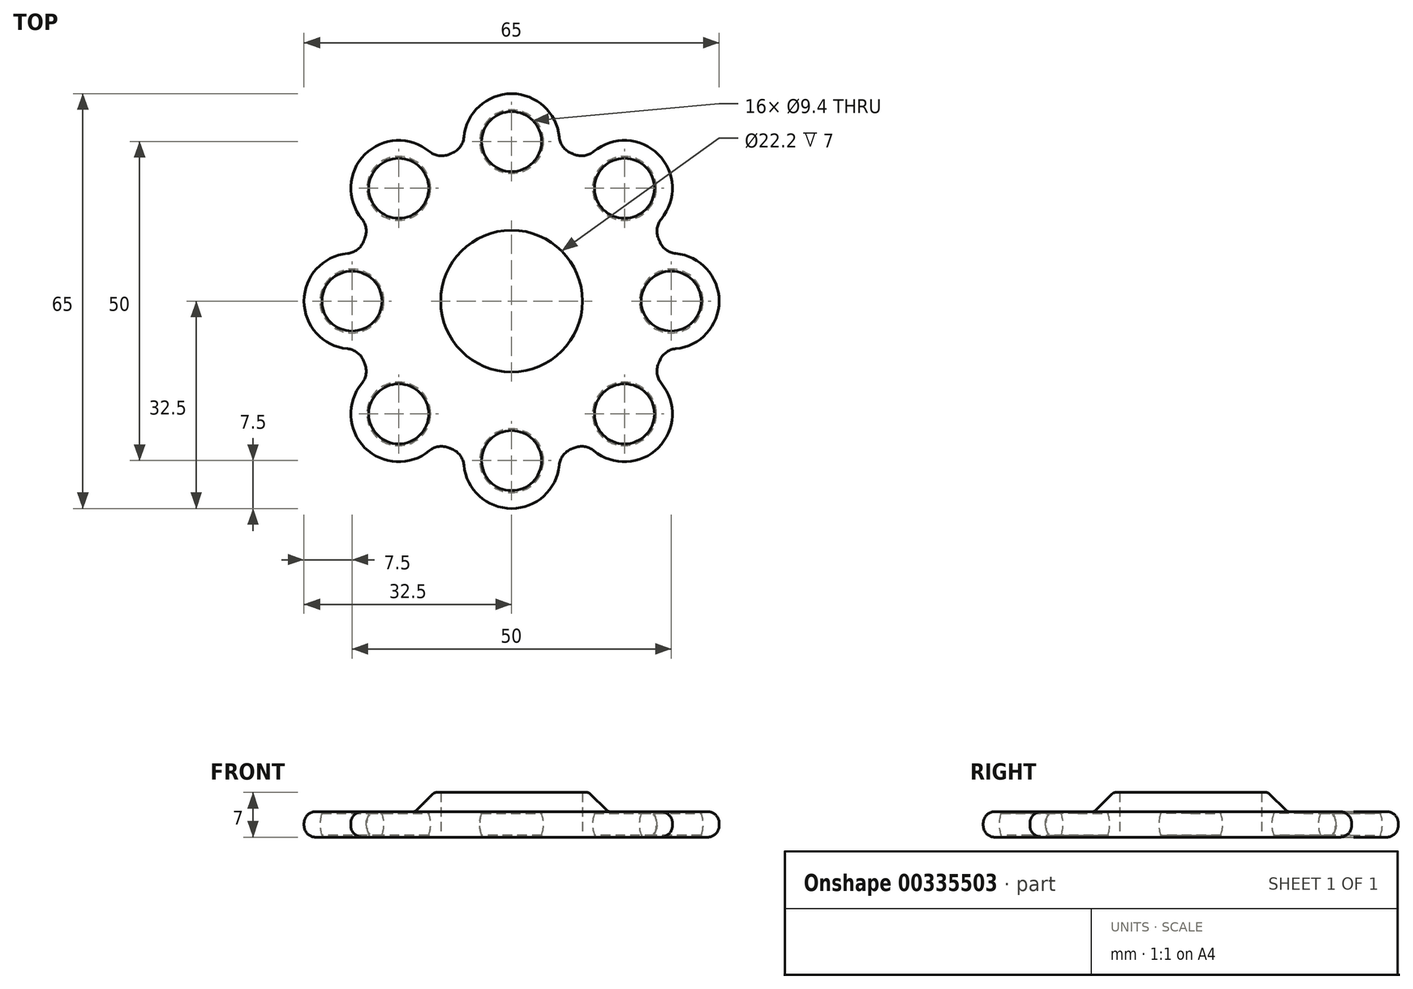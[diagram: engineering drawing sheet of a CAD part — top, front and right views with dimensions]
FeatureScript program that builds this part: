
annotation { "Feature Type Name" : "Feature", "Feature Type Description" : "" }
export const myFeature = defineFeature(function(context is Context, id is Id, definition is map)
    precondition{}
    {
        {
            var Q0;
            Q0=qCreatedBy(makeId("Top.planeOp"),FACE);
            var sketch = newSketch(context, id + "F0", { "sketchPlane" : qUnion([Q0])});
            skCircle(sketch, "E0", {"center": v(0, 0) * mm, "radius": 11.1 * mm});
            skPoint(sketch, "E1.0.midPoint", {"position": v(12.23, 6.82) * mm});
            skCircle(sketch, "E2", {"center": v(0, 25) * mm, "radius": 4.7 * mm});
            skCircle(sketch, "E3.1.0", {"center": v(-17.68, 17.68) * mm, "radius": 4.7 * mm});
            skCircle(sketch, "E3.2.0", {"center": v(-25, 0) * mm, "radius": 4.7 * mm});
            skCircle(sketch, "E3.3.0", {"center": v(-17.68, -17.68) * mm, "radius": 4.7 * mm});
            skCircle(sketch, "E3.4.0", {"center": v(0, -25) * mm, "radius": 4.7 * mm});
            skCircle(sketch, "E3.5.0", {"center": v(17.68, -17.68) * mm, "radius": 4.7 * mm});
            skCircle(sketch, "E3.6.0", {"center": v(25, 0) * mm, "radius": 4.7 * mm});
            skCircle(sketch, "E3.7.0", {"center": v(17.68, 17.68) * mm, "radius": 4.7 * mm});
            skCircle(sketch, "E4", {"center": v(0, 25) * mm, "radius": 7.5 * mm});
            skCircle(sketch, "E5.1.0", {"center": v(-17.68, 17.68) * mm, "radius": 7.5 * mm});
            skCircle(sketch, "E5.2.0", {"center": v(-25, 0) * mm, "radius": 7.5 * mm});
            skCircle(sketch, "E5.3.0", {"center": v(-17.68, -17.68) * mm, "radius": 7.5 * mm});
            skCircle(sketch, "E5.4.0", {"center": v(0, -25) * mm, "radius": 7.5 * mm});
            skCircle(sketch, "E5.5.0", {"center": v(17.68, -17.68) * mm, "radius": 7.5 * mm});
            skCircle(sketch, "E5.6.0", {"center": v(25, 0) * mm, "radius": 7.5 * mm});
            skCircle(sketch, "E5.7.0", {"center": v(17.68, 17.68) * mm, "radius": 7.5 * mm});
            skCircle(sketch, "E6", {"center": v(0, 0) * mm, "radius": 25 * mm});
            skSolve(sketch);
        }
        {
            var Q0;
            Q0=makeQuery(id+"F0.imprint","IMPRINT",FACE,{"disambiguationData":[TD([[makeQuery(id+"F0.imprint","IMPRINT",EDGE,{"derivedFrom":sQuery(id+"F0.wireOp",EDGE,"E0")}),-1.0]])]});
            var Q1;
            {var subQ0=sQuery(id+"F0.wireOp",EDGE,"E6");var subQ1=sQuery(id+"F0.wireOp",EDGE,"E3.3.0");var subQ2=makeQuery(id+"F0.imprint","INTERSECT",VERTEX,{"disambiguationData":[OD(0.0)],"derivedFrom":[subQ1,subQ0]});Q1=makeQuery(id+"F0.imprint","IMPRINT",FACE,{"disambiguationData":[TD([[makeQuery(id+"F0.imprint","IMPRINT",EDGE,{"disambiguationData":[TD([[subQ2,-1.0]])],"derivedFrom":subQ1}),-1.0]])]});}
            var Q2;
            {var subQ0=sQuery(id+"F0.wireOp",EDGE,"E6");var subQ1=sQuery(id+"F0.wireOp",EDGE,"E3.3.0");var subQ2=makeQuery(id+"F0.imprint","INTERSECT",VERTEX,{"disambiguationData":[OD(0.0)],"derivedFrom":[subQ1,subQ0]});Q2=makeQuery(id+"F0.imprint","IMPRINT",FACE,{"disambiguationData":[TD([[makeQuery(id+"F0.imprint","IMPRINT",EDGE,{"disambiguationData":[TD([[subQ2,1.0]])],"derivedFrom":subQ1}),-1.0]])]});}
            var Q3;
            {var subQ0=sQuery(id+"F0.wireOp",EDGE,"E6");var subQ1=sQuery(id+"F0.wireOp",EDGE,"E3.2.0");var subQ2=makeQuery(id+"F0.imprint","INTERSECT",VERTEX,{"disambiguationData":[OD(0.0)],"derivedFrom":[subQ1,subQ0]});Q3=makeQuery(id+"F0.imprint","IMPRINT",FACE,{"disambiguationData":[TD([[makeQuery(id+"F0.imprint","IMPRINT",EDGE,{"disambiguationData":[TD([[subQ2,1.0]])],"derivedFrom":subQ1}),-1.0]])]});}
            var Q4;
            {var subQ0=sQuery(id+"F0.wireOp",EDGE,"E6");var subQ1=sQuery(id+"F0.wireOp",EDGE,"E3.2.0");var subQ2=makeQuery(id+"F0.imprint","INTERSECT",VERTEX,{"disambiguationData":[OD(0.0)],"derivedFrom":[subQ1,subQ0]});Q4=makeQuery(id+"F0.imprint","IMPRINT",FACE,{"disambiguationData":[TD([[makeQuery(id+"F0.imprint","IMPRINT",EDGE,{"disambiguationData":[TD([[subQ2,-1.0]])],"derivedFrom":subQ1}),-1.0]])]});}
            var Q5;
            {var subQ0=sQuery(id+"F0.wireOp",EDGE,"E6");var subQ1=sQuery(id+"F0.wireOp",EDGE,"E3.1.0");var subQ2=makeQuery(id+"F0.imprint","INTERSECT",VERTEX,{"disambiguationData":[OD(0.0)],"derivedFrom":[subQ1,subQ0]});Q5=makeQuery(id+"F0.imprint","IMPRINT",FACE,{"disambiguationData":[TD([[makeQuery(id+"F0.imprint","IMPRINT",EDGE,{"disambiguationData":[TD([[subQ2,-1.0]])],"derivedFrom":subQ1}),-1.0]])]});}
            var Q6;
            {var subQ0=sQuery(id+"F0.wireOp",EDGE,"E6");var subQ1=sQuery(id+"F0.wireOp",EDGE,"E3.1.0");var subQ2=makeQuery(id+"F0.imprint","INTERSECT",VERTEX,{"disambiguationData":[OD(0.0)],"derivedFrom":[subQ1,subQ0]});Q6=makeQuery(id+"F0.imprint","IMPRINT",FACE,{"disambiguationData":[TD([[makeQuery(id+"F0.imprint","IMPRINT",EDGE,{"disambiguationData":[TD([[subQ2,1.0]])],"derivedFrom":subQ1}),-1.0]])]});}
            var Q7;
            {var subQ0=sQuery(id+"F0.wireOp",EDGE,"E6");var subQ1=sQuery(id+"F0.wireOp",EDGE,"E2");var subQ2=makeQuery(id+"F0.imprint","INTERSECT",VERTEX,{"disambiguationData":[OD(0.0)],"derivedFrom":[subQ1,subQ0]});Q7=makeQuery(id+"F0.imprint","IMPRINT",FACE,{"disambiguationData":[TD([[makeQuery(id+"F0.imprint","IMPRINT",EDGE,{"disambiguationData":[TD([[subQ2,1.0]])],"derivedFrom":subQ1}),-1.0]])]});}
            var Q8;
            {var subQ0=sQuery(id+"F0.wireOp",EDGE,"E6");var subQ1=sQuery(id+"F0.wireOp",EDGE,"E2");var subQ2=makeQuery(id+"F0.imprint","INTERSECT",VERTEX,{"disambiguationData":[OD(0.0)],"derivedFrom":[subQ1,subQ0]});Q8=makeQuery(id+"F0.imprint","IMPRINT",FACE,{"disambiguationData":[TD([[makeQuery(id+"F0.imprint","IMPRINT",EDGE,{"disambiguationData":[TD([[subQ2,-1.0]])],"derivedFrom":subQ1}),-1.0]])]});}
            var Q9;
            {var subQ0=sQuery(id+"F0.wireOp",EDGE,"E6");var subQ1=sQuery(id+"F0.wireOp",EDGE,"E3.7.0");var subQ2=makeQuery(id+"F0.imprint","INTERSECT",VERTEX,{"disambiguationData":[OD(0.0)],"derivedFrom":[subQ1,subQ0]});Q9=makeQuery(id+"F0.imprint","IMPRINT",FACE,{"disambiguationData":[TD([[makeQuery(id+"F0.imprint","IMPRINT",EDGE,{"disambiguationData":[TD([[subQ2,1.0]])],"derivedFrom":subQ1}),-1.0]])]});}
            var Q10;
            {var subQ0=sQuery(id+"F0.wireOp",EDGE,"E6");var subQ1=sQuery(id+"F0.wireOp",EDGE,"E3.7.0");var subQ2=makeQuery(id+"F0.imprint","INTERSECT",VERTEX,{"disambiguationData":[OD(0.0)],"derivedFrom":[subQ1,subQ0]});Q10=makeQuery(id+"F0.imprint","IMPRINT",FACE,{"disambiguationData":[TD([[makeQuery(id+"F0.imprint","IMPRINT",EDGE,{"disambiguationData":[TD([[subQ2,-1.0]])],"derivedFrom":subQ1}),-1.0]])]});}
            var Q11;
            {var subQ0=sQuery(id+"F0.wireOp",EDGE,"E6");var subQ1=sQuery(id+"F0.wireOp",EDGE,"E3.6.0");var subQ2=makeQuery(id+"F0.imprint","INTERSECT",VERTEX,{"disambiguationData":[OD(0.0)],"derivedFrom":[subQ1,subQ0]});Q11=makeQuery(id+"F0.imprint","IMPRINT",FACE,{"disambiguationData":[TD([[makeQuery(id+"F0.imprint","IMPRINT",EDGE,{"disambiguationData":[TD([[subQ2,-1.0]])],"derivedFrom":subQ1}),-1.0]])]});}
            var Q12;
            {var subQ0=sQuery(id+"F0.wireOp",EDGE,"E6");var subQ1=sQuery(id+"F0.wireOp",EDGE,"E3.6.0");var subQ2=makeQuery(id+"F0.imprint","INTERSECT",VERTEX,{"disambiguationData":[OD(0.0)],"derivedFrom":[subQ1,subQ0]});Q12=makeQuery(id+"F0.imprint","IMPRINT",FACE,{"disambiguationData":[TD([[makeQuery(id+"F0.imprint","IMPRINT",EDGE,{"disambiguationData":[TD([[subQ2,1.0]])],"derivedFrom":subQ1}),-1.0]])]});}
            var Q13;
            {var subQ0=sQuery(id+"F0.wireOp",EDGE,"E6");var subQ1=sQuery(id+"F0.wireOp",EDGE,"E3.5.0");var subQ2=makeQuery(id+"F0.imprint","INTERSECT",VERTEX,{"disambiguationData":[OD(0.0)],"derivedFrom":[subQ1,subQ0]});Q13=makeQuery(id+"F0.imprint","IMPRINT",FACE,{"disambiguationData":[TD([[makeQuery(id+"F0.imprint","IMPRINT",EDGE,{"disambiguationData":[TD([[subQ2,1.0]])],"derivedFrom":subQ1}),-1.0]])]});}
            var Q14;
            {var subQ0=sQuery(id+"F0.wireOp",EDGE,"E6");var subQ1=sQuery(id+"F0.wireOp",EDGE,"E3.5.0");var subQ2=makeQuery(id+"F0.imprint","INTERSECT",VERTEX,{"disambiguationData":[OD(0.0)],"derivedFrom":[subQ1,subQ0]});Q14=makeQuery(id+"F0.imprint","IMPRINT",FACE,{"disambiguationData":[TD([[makeQuery(id+"F0.imprint","IMPRINT",EDGE,{"disambiguationData":[TD([[subQ2,-1.0]])],"derivedFrom":subQ1}),-1.0]])]});}
            var Q15;
            {var subQ0=sQuery(id+"F0.wireOp",EDGE,"E6");var subQ1=sQuery(id+"F0.wireOp",EDGE,"E3.4.0");var subQ2=makeQuery(id+"F0.imprint","INTERSECT",VERTEX,{"disambiguationData":[OD(0.0)],"derivedFrom":[subQ1,subQ0]});Q15=makeQuery(id+"F0.imprint","IMPRINT",FACE,{"disambiguationData":[TD([[makeQuery(id+"F0.imprint","IMPRINT",EDGE,{"disambiguationData":[TD([[subQ2,1.0]])],"derivedFrom":subQ1}),-1.0]])]});}
            var Q16;
            {var subQ0=sQuery(id+"F0.wireOp",EDGE,"E6");var subQ1=sQuery(id+"F0.wireOp",EDGE,"E3.4.0");var subQ2=makeQuery(id+"F0.imprint","INTERSECT",VERTEX,{"disambiguationData":[OD(0.0)],"derivedFrom":[subQ1,subQ0]});Q16=makeQuery(id+"F0.imprint","IMPRINT",FACE,{"disambiguationData":[TD([[makeQuery(id+"F0.imprint","IMPRINT",EDGE,{"disambiguationData":[TD([[subQ2,-1.0]])],"derivedFrom":subQ1}),-1.0]])]});}
            extrude(context, id + "F1", {"entities" : qUnion([Q0, Q1, Q2, Q3, Q4, Q5, Q6, Q7, Q8, Q9, Q10, Q11, Q12, Q13, Q14, Q15, Q16]), "depth" : 2 * mm, "hasSecondDirection" : true, "secondDirectionOppositeDirection" : true, "secondDirectionDepth" : 2 * mm});
        }
        {
            var Q0;
            {var subQ0=sQuery(id+"F0.wireOp",EDGE,"E6");var subQ1=sQuery(id+"F0.wireOp",EDGE,"E5.4.0");Q0=makeQuery(id+"F1.opExtrude","SWEPT_EDGE",EDGE,{"disambiguationData":[OSD([subQ1,subQ0]),TDD([makeQuery(id+"F0.imprint","INTERSECT",VERTEX,{"disambiguationData":[OD(0.0)],"derivedFrom":[subQ1,subQ0]})])]});}
            var Q1;
            {var subQ0=sQuery(id+"F0.wireOp",EDGE,"E6");var subQ1=sQuery(id+"F0.wireOp",EDGE,"E5.2.0");Q1=makeQuery(id+"F1.opExtrude","SWEPT_EDGE",EDGE,{"disambiguationData":[OSD([subQ1,subQ0]),TDD([makeQuery(id+"F0.imprint","INTERSECT",VERTEX,{"disambiguationData":[OD(1.0)],"derivedFrom":[subQ1,subQ0]})])]});}
            var Q2;
            {var subQ0=sQuery(id+"F0.wireOp",EDGE,"E6");var subQ1=sQuery(id+"F0.wireOp",EDGE,"E5.2.0");Q2=makeQuery(id+"F1.opExtrude","SWEPT_EDGE",EDGE,{"disambiguationData":[OSD([subQ1,subQ0]),TDD([makeQuery(id+"F0.imprint","INTERSECT",VERTEX,{"disambiguationData":[OD(0.0)],"derivedFrom":[subQ1,subQ0]})])]});}
            var Q3;
            {var subQ0=sQuery(id+"F0.wireOp",EDGE,"E6");var subQ1=sQuery(id+"F0.wireOp",EDGE,"E4");Q3=makeQuery(id+"F1.opExtrude","SWEPT_EDGE",EDGE,{"disambiguationData":[OSD([subQ1,subQ0]),TDD([makeQuery(id+"F0.imprint","INTERSECT",VERTEX,{"disambiguationData":[OD(1.0)],"derivedFrom":[subQ1,subQ0]})])]});}
            var Q4;
            {var subQ0=sQuery(id+"F0.wireOp",EDGE,"E6");var subQ1=sQuery(id+"F0.wireOp",EDGE,"E5.7.0");Q4=makeQuery(id+"F1.opExtrude","SWEPT_EDGE",EDGE,{"disambiguationData":[OSD([subQ1,subQ0]),TDD([makeQuery(id+"F0.imprint","INTERSECT",VERTEX,{"disambiguationData":[OD(1.0)],"derivedFrom":[subQ1,subQ0]})])]});}
            var Q5;
            {var subQ0=sQuery(id+"F0.wireOp",EDGE,"E6");var subQ1=sQuery(id+"F0.wireOp",EDGE,"E5.1.0");Q5=makeQuery(id+"F1.opExtrude","SWEPT_EDGE",EDGE,{"disambiguationData":[OSD([subQ1,subQ0]),TDD([makeQuery(id+"F0.imprint","INTERSECT",VERTEX,{"disambiguationData":[OD(1.0)],"derivedFrom":[subQ1,subQ0]})])]});}
            var Q6;
            {var subQ0=sQuery(id+"F0.wireOp",EDGE,"E6");var subQ1=sQuery(id+"F0.wireOp",EDGE,"E5.3.0");Q6=makeQuery(id+"F1.opExtrude","SWEPT_EDGE",EDGE,{"disambiguationData":[OSD([subQ1,subQ0]),TDD([makeQuery(id+"F0.imprint","INTERSECT",VERTEX,{"disambiguationData":[OD(0.0)],"derivedFrom":[subQ1,subQ0]})])]});}
            var Q7;
            {var subQ0=sQuery(id+"F0.wireOp",EDGE,"E6");var subQ1=sQuery(id+"F0.wireOp",EDGE,"E5.1.0");Q7=makeQuery(id+"F1.opExtrude","SWEPT_EDGE",EDGE,{"disambiguationData":[OSD([subQ1,subQ0]),TDD([makeQuery(id+"F0.imprint","INTERSECT",VERTEX,{"disambiguationData":[OD(0.0)],"derivedFrom":[subQ1,subQ0]})])]});}
            var Q8;
            {var subQ0=sQuery(id+"F0.wireOp",EDGE,"E6");var subQ1=sQuery(id+"F0.wireOp",EDGE,"E4");Q8=makeQuery(id+"F1.opExtrude","SWEPT_EDGE",EDGE,{"disambiguationData":[OSD([subQ1,subQ0]),TDD([makeQuery(id+"F0.imprint","INTERSECT",VERTEX,{"disambiguationData":[OD(0.0)],"derivedFrom":[subQ1,subQ0]})])]});}
            var Q9;
            {var subQ0=sQuery(id+"F0.wireOp",EDGE,"E6");var subQ1=sQuery(id+"F0.wireOp",EDGE,"E5.6.0");Q9=makeQuery(id+"F1.opExtrude","SWEPT_EDGE",EDGE,{"disambiguationData":[OSD([subQ1,subQ0]),TDD([makeQuery(id+"F0.imprint","INTERSECT",VERTEX,{"disambiguationData":[OD(0.0)],"derivedFrom":[subQ1,subQ0]})])]});}
            var Q10;
            {var subQ0=sQuery(id+"F0.wireOp",EDGE,"E6");var subQ1=sQuery(id+"F0.wireOp",EDGE,"E5.7.0");Q10=makeQuery(id+"F1.opExtrude","SWEPT_EDGE",EDGE,{"disambiguationData":[OSD([subQ1,subQ0]),TDD([makeQuery(id+"F0.imprint","INTERSECT",VERTEX,{"disambiguationData":[OD(0.0)],"derivedFrom":[subQ1,subQ0]})])]});}
            var Q11;
            {var subQ0=sQuery(id+"F0.wireOp",EDGE,"E6");var subQ1=sQuery(id+"F0.wireOp",EDGE,"E5.6.0");Q11=makeQuery(id+"F1.opExtrude","SWEPT_EDGE",EDGE,{"disambiguationData":[OSD([subQ1,subQ0]),TDD([makeQuery(id+"F0.imprint","INTERSECT",VERTEX,{"disambiguationData":[OD(1.0)],"derivedFrom":[subQ1,subQ0]})])]});}
            var Q12;
            {var subQ0=sQuery(id+"F0.wireOp",EDGE,"E6");var subQ1=sQuery(id+"F0.wireOp",EDGE,"E5.5.0");Q12=makeQuery(id+"F1.opExtrude","SWEPT_EDGE",EDGE,{"disambiguationData":[OSD([subQ1,subQ0]),TDD([makeQuery(id+"F0.imprint","INTERSECT",VERTEX,{"disambiguationData":[OD(1.0)],"derivedFrom":[subQ1,subQ0]})])]});}
            var Q13;
            {var subQ0=sQuery(id+"F0.wireOp",EDGE,"E6");var subQ1=sQuery(id+"F0.wireOp",EDGE,"E5.5.0");Q13=makeQuery(id+"F1.opExtrude","SWEPT_EDGE",EDGE,{"disambiguationData":[OSD([subQ1,subQ0]),TDD([makeQuery(id+"F0.imprint","INTERSECT",VERTEX,{"disambiguationData":[OD(0.0)],"derivedFrom":[subQ1,subQ0]})])]});}
            var Q14;
            {var subQ0=sQuery(id+"F0.wireOp",EDGE,"E6");var subQ1=sQuery(id+"F0.wireOp",EDGE,"E5.4.0");Q14=makeQuery(id+"F1.opExtrude","SWEPT_EDGE",EDGE,{"disambiguationData":[OSD([subQ1,subQ0]),TDD([makeQuery(id+"F0.imprint","INTERSECT",VERTEX,{"disambiguationData":[OD(1.0)],"derivedFrom":[subQ1,subQ0]})])]});}
            var Q15;
            {var subQ0=sQuery(id+"F0.wireOp",EDGE,"E6");var subQ1=sQuery(id+"F0.wireOp",EDGE,"E5.3.0");Q15=makeQuery(id+"F1.opExtrude","SWEPT_EDGE",EDGE,{"disambiguationData":[OSD([subQ1,subQ0]),TDD([makeQuery(id+"F0.imprint","INTERSECT",VERTEX,{"disambiguationData":[OD(1.0)],"derivedFrom":[subQ1,subQ0]})])]});}
            fillet(context, id + "F2", {"entities" : qUnion([Q0, Q1, Q2, Q3, Q4, Q5, Q6, Q7, Q8, Q9, Q10, Q11, Q12, Q13, Q14, Q15]), "radius" : 3 * mm, "tangentPropagation" : true, "allowEdgeOverflow" : false});
        }
        {
            var Q0;
            Q0=makeQuery(id+"F1.opExtrude","CAP_EDGE",EDGE,{"disambiguationData":[OSD([sQuery(id+"F0.wireOp",EDGE,"E5.7.0")])],"isStart":false});
            var Q1;
            Q1=makeQuery(id+"F1.opExtrude","CAP_EDGE",EDGE,{"disambiguationData":[OSD([sQuery(id+"F0.wireOp",EDGE,"E5.7.0")])],"isStart":true});
            fillet(context, id + "F3", {"entities" : qUnion([Q0, Q1]), "radius" : 1.8 * mm, "tangentPropagation" : true, "allowEdgeOverflow" : false});
        }
        {
            var Q0;
            Q0=qCreatedBy(makeId("Right.planeOp"),FACE);
            var sketch = newSketch(context, id + "F4", { "sketchPlane" : qUnion([Q0])});
            skPoint(sketch, "E7.0", {"position": v(-25, 0) * mm});
            skPoint(sketch, "E7.1", {"position": v(25, 0) * mm});
            skLineSegment(sketch, "E8", {"start": v(-25, 12.35) * mm, "end": v(-25, -14.21) * mm, "construction": true});
            skLineSegment(sketch, "E9", {"start": v(25, 12.16) * mm, "end": v(25, -14.21) * mm, "construction": true});
            skPoint(sketch, "E10", {"position": v(-25, 5) * mm});
            skPoint(sketch, "E11", {"position": v(-25, -5) * mm});
            skPoint(sketch, "E12", {"position": v(25, 5) * mm});
            skPoint(sketch, "E13", {"position": v(25, -5) * mm});
            skArc(sketch, "E14", {"start": v(-25, 5) * mm, "mid": v(-30, 0) * mm, "end": v(-25, -5) * mm});
            skArc(sketch, "E15", {"start": v(25, -5) * mm, "mid": v(30, 0) * mm, "end": v(25, 5) * mm});
            skLineSegment(sketch, "E16", {"start": v(-25, 5) * mm, "end": v(-25, -5) * mm});
            skLineSegment(sketch, "E17", {"start": v(25, 5) * mm, "end": v(25, -5) * mm});
            skLineSegment(sketch, "E18", {"start": v(0, 41.23) * mm, "end": v(0, -49.38) * mm, "construction": true});
            skSolve(sketch);
        }
        {
            var Q0;
            Q0=makeQuery(id+"F4.imprint","IMPRINT",FACE,{"disambiguationData":[TD([[makeQuery(id+"F4.imprint","IMPRINT",EDGE,{"derivedFrom":sQuery(id+"F4.wireOp",EDGE,"E14")}),1.0]])]});
            var Q1;
            Q1=sQuery(id+"F4.wireOp",EDGE,"E8");
            revolve(context, id + "F5", {"entities" : qUnion([Q0]), "axis" : qUnion([Q1]), "revolveType" : RevolveType.FULL});
        }
        {
            var Q0;
            Q0=makeQuery(id+"F4.imprint","IMPRINT",FACE,{"disambiguationData":[TD([[makeQuery(id+"F4.imprint","IMPRINT",EDGE,{"derivedFrom":sQuery(id+"F4.wireOp",EDGE,"E15")}),1.0]])]});
            var Q1;
            Q1=sQuery(id+"F4.wireOp",EDGE,"E9");
            revolve(context, id + "F6", {"entities" : qUnion([Q0]), "axis" : qUnion([Q1]), "revolveType" : RevolveType.FULL});
        }
        {
            var Q0;
            Q0=makeQuery(id+"F6.opRevolve","SWEPT_BODY",BODY,{"disambiguationData":[OSD([sQuery(id+"F4.wireOp",EDGE,"E15"),sQuery(id+"F4.wireOp",EDGE,"E17")])]});
            var Q1;
            Q1=makeQuery(id+"F5.opRevolve","SWEPT_BODY",BODY,{"disambiguationData":[OSD([sQuery(id+"F4.wireOp",EDGE,"E14"),sQuery(id+"F4.wireOp",EDGE,"E16")])]});
            var Q2;
            Q2=makeQuery(id+"F1.opExtrude","SWEPT_BODY",BODY,{"disambiguationData":[OSD([sQuery(id+"F0.wireOp",EDGE,"E0"),sQuery(id+"F0.wireOp",EDGE,"E2"),sQuery(id+"F0.wireOp",EDGE,"E3.1.0"),sQuery(id+"F0.wireOp",EDGE,"E3.2.0"),sQuery(id+"F0.wireOp",EDGE,"E3.3.0"),sQuery(id+"F0.wireOp",EDGE,"E3.4.0"),sQuery(id+"F0.wireOp",EDGE,"E3.5.0"),sQuery(id+"F0.wireOp",EDGE,"E3.6.0"),sQuery(id+"F0.wireOp",EDGE,"E3.7.0"),sQuery(id+"F0.wireOp",EDGE,"E4"),sQuery(id+"F0.wireOp",EDGE,"E5.1.0"),sQuery(id+"F0.wireOp",EDGE,"E5.2.0"),sQuery(id+"F0.wireOp",EDGE,"E5.3.0"),sQuery(id+"F0.wireOp",EDGE,"E5.4.0"),sQuery(id+"F0.wireOp",EDGE,"E5.5.0"),sQuery(id+"F0.wireOp",EDGE,"E5.6.0"),sQuery(id+"F0.wireOp",EDGE,"E5.7.0"),sQuery(id+"F0.wireOp",EDGE,"E6")])]});
            booleanBodies(context, id + "F7", {"operationType" : BooleanOperationType.SUBTRACTION, "tools" : qUnion([Q0, Q1]), "targets" : qUnion([Q2])});
        }
        {
            var Q0;
            Q0=qCreatedBy(makeId("Front.planeOp"),FACE);
            var sketch = newSketch(context, id + "F8", { "sketchPlane" : qUnion([Q0])});
            skPoint(sketch, "E19.0", {"position": v(-25, 0) * mm});
            skPoint(sketch, "E19.1", {"position": v(25, 0) * mm});
            skLineSegment(sketch, "E20", {"start": v(-25, 18.9) * mm, "end": v(-25, -20.91) * mm, "construction": true});
            skLineSegment(sketch, "E21", {"start": v(25, 20.02) * mm, "end": v(25, -22.02) * mm, "construction": true});
            skPoint(sketch, "E22", {"position": v(-25, 5) * mm});
            skPoint(sketch, "E23", {"position": v(-25, -5) * mm});
            skPoint(sketch, "E24", {"position": v(25, 5) * mm});
            skPoint(sketch, "E25", {"position": v(25, -5) * mm});
            skArc(sketch, "E26", {"start": v(-25, 5) * mm, "mid": v(-30, 0) * mm, "end": v(-25, -5) * mm});
            skArc(sketch, "E27", {"start": v(25, -5) * mm, "mid": v(30, 0) * mm, "end": v(25, 5) * mm});
            skLineSegment(sketch, "E28", {"start": v(-25, 5) * mm, "end": v(-25, -5) * mm});
            skLineSegment(sketch, "E29", {"start": v(25, 5) * mm, "end": v(25, -5) * mm});
            skSolve(sketch);
        }
        {
            var Q0;
            Q0=makeQuery(id+"F8.imprint","IMPRINT",FACE,{"disambiguationData":[TD([[makeQuery(id+"F8.imprint","IMPRINT",EDGE,{"derivedFrom":sQuery(id+"F8.wireOp",EDGE,"E26")}),1.0]])]});
            var Q1;
            Q1=sQuery(id+"F8.wireOp",EDGE,"E20");
            revolve(context, id + "F9", {"entities" : qUnion([Q0]), "axis" : qUnion([Q1]), "revolveType" : RevolveType.FULL});
        }
        {
            var Q0;
            Q0=makeQuery(id+"F8.imprint","IMPRINT",FACE,{"disambiguationData":[TD([[makeQuery(id+"F8.imprint","IMPRINT",EDGE,{"derivedFrom":sQuery(id+"F8.wireOp",EDGE,"E27")}),1.0]])]});
            var Q1;
            Q1=sQuery(id+"F8.wireOp",EDGE,"E21");
            revolve(context, id + "F10", {"entities" : qUnion([Q0]), "axis" : qUnion([Q1]), "revolveType" : RevolveType.FULL});
        }
        {
            var Q0;
            Q0=makeQuery(id+"F9.opRevolve","SWEPT_BODY",BODY,{"disambiguationData":[OSD([sQuery(id+"F8.wireOp",EDGE,"E26"),sQuery(id+"F8.wireOp",EDGE,"E28")])]});
            var Q1;
            Q1=makeQuery(id+"F10.opRevolve","SWEPT_BODY",BODY,{"disambiguationData":[OSD([sQuery(id+"F8.wireOp",EDGE,"E27"),sQuery(id+"F8.wireOp",EDGE,"E29")])]});
            var Q2;
            Q2=makeQuery(id+"F1.opExtrude","SWEPT_BODY",BODY,{"disambiguationData":[OSD([sQuery(id+"F0.wireOp",EDGE,"E0"),sQuery(id+"F0.wireOp",EDGE,"E2"),sQuery(id+"F0.wireOp",EDGE,"E3.1.0"),sQuery(id+"F0.wireOp",EDGE,"E3.2.0"),sQuery(id+"F0.wireOp",EDGE,"E3.3.0"),sQuery(id+"F0.wireOp",EDGE,"E3.4.0"),sQuery(id+"F0.wireOp",EDGE,"E3.5.0"),sQuery(id+"F0.wireOp",EDGE,"E3.6.0"),sQuery(id+"F0.wireOp",EDGE,"E3.7.0"),sQuery(id+"F0.wireOp",EDGE,"E4"),sQuery(id+"F0.wireOp",EDGE,"E5.1.0"),sQuery(id+"F0.wireOp",EDGE,"E5.2.0"),sQuery(id+"F0.wireOp",EDGE,"E5.3.0"),sQuery(id+"F0.wireOp",EDGE,"E5.4.0"),sQuery(id+"F0.wireOp",EDGE,"E5.5.0"),sQuery(id+"F0.wireOp",EDGE,"E5.6.0"),sQuery(id+"F0.wireOp",EDGE,"E5.7.0"),sQuery(id+"F0.wireOp",EDGE,"E6")])]});
            booleanBodies(context, id + "F11", {"operationType" : BooleanOperationType.SUBTRACTION, "tools" : qUnion([Q0, Q1]), "targets" : qUnion([Q2])});
        }
        {
            var Q0;
            Q0=qCreatedBy(makeId("Front.planeOp"),FACE);
            var Q1;
            Q1=sQuery(id+"F0.wireOp",VERTEX,"E3.3.0.center");
            cPlane(context, id + "F12", {"entities" : qUnion([Q0, Q1]), "cplaneType" : CPlaneType.PLANE_POINT, "offset" : 25 * mm, "width" : 150 * mm, "height" : 150 * mm});
        }
        {
            var Q0;
            Q0=qCreatedBy(id+"F12.planeOp",FACE);
            var sketch = newSketch(context, id + "F13", { "sketchPlane" : qUnion([Q0])});
            skPoint(sketch, "E30.0", {"position": v(-17.68, 0) * mm});
            skPoint(sketch, "E30.1", {"position": v(17.68, 0) * mm});
            skLineSegment(sketch, "E31", {"start": v(-17.68, 20.76) * mm, "end": v(-17.68, -25.8) * mm, "construction": true});
            skLineSegment(sketch, "E32", {"start": v(17.68, 18.25) * mm, "end": v(17.68, -22.97) * mm, "construction": true});
            skPoint(sketch, "E33", {"position": v(-17.68, 5) * mm});
            skPoint(sketch, "E34", {"position": v(-17.68, -5) * mm});
            skPoint(sketch, "E35", {"position": v(17.68, -5) * mm});
            skPoint(sketch, "E36", {"position": v(17.68, 5) * mm});
            skArc(sketch, "E37", {"start": v(-17.68, 5) * mm, "mid": v(-22.68, 0) * mm, "end": v(-17.68, -5) * mm});
            skArc(sketch, "E38", {"start": v(17.68, -5) * mm, "mid": v(22.68, 0) * mm, "end": v(17.68, 5) * mm});
            skLineSegment(sketch, "E39", {"start": v(-17.68, 5) * mm, "end": v(-17.68, -5) * mm});
            skLineSegment(sketch, "E40", {"start": v(17.68, 5) * mm, "end": v(17.68, -5) * mm});
            skSolve(sketch);
        }
        {
            var Q0;
            Q0=makeQuery(id+"F13.imprint","IMPRINT",FACE,{"disambiguationData":[TD([[makeQuery(id+"F13.imprint","IMPRINT",EDGE,{"derivedFrom":sQuery(id+"F13.wireOp",EDGE,"E37")}),1.0]])]});
            var Q1;
            Q1=sQuery(id+"F13.wireOp",EDGE,"E31");
            revolve(context, id + "F14", {"entities" : qUnion([Q0]), "axis" : qUnion([Q1]), "revolveType" : RevolveType.FULL});
        }
        {
            var Q0;
            Q0=makeQuery(id+"F13.imprint","IMPRINT",FACE,{"disambiguationData":[TD([[makeQuery(id+"F13.imprint","IMPRINT",EDGE,{"derivedFrom":sQuery(id+"F13.wireOp",EDGE,"E38")}),1.0]])]});
            var Q1;
            Q1=sQuery(id+"F13.wireOp",EDGE,"E32");
            revolve(context, id + "F15", {"entities" : qUnion([Q0]), "axis" : qUnion([Q1]), "revolveType" : RevolveType.FULL});
        }
        {
            var Q0;
            Q0=makeQuery(id+"F15.opRevolve","SWEPT_BODY",BODY,{"disambiguationData":[OSD([sQuery(id+"F13.wireOp",EDGE,"E38"),sQuery(id+"F13.wireOp",EDGE,"E40")])]});
            var Q1;
            Q1=makeQuery(id+"F14.opRevolve","SWEPT_BODY",BODY,{"disambiguationData":[OSD([sQuery(id+"F13.wireOp",EDGE,"E37"),sQuery(id+"F13.wireOp",EDGE,"E39")])]});
            var Q2;
            Q2=makeQuery(id+"F1.opExtrude","SWEPT_BODY",BODY,{"disambiguationData":[OSD([sQuery(id+"F0.wireOp",EDGE,"E0"),sQuery(id+"F0.wireOp",EDGE,"E2"),sQuery(id+"F0.wireOp",EDGE,"E3.1.0"),sQuery(id+"F0.wireOp",EDGE,"E3.2.0"),sQuery(id+"F0.wireOp",EDGE,"E3.3.0"),sQuery(id+"F0.wireOp",EDGE,"E3.4.0"),sQuery(id+"F0.wireOp",EDGE,"E3.5.0"),sQuery(id+"F0.wireOp",EDGE,"E3.6.0"),sQuery(id+"F0.wireOp",EDGE,"E3.7.0"),sQuery(id+"F0.wireOp",EDGE,"E4"),sQuery(id+"F0.wireOp",EDGE,"E5.1.0"),sQuery(id+"F0.wireOp",EDGE,"E5.2.0"),sQuery(id+"F0.wireOp",EDGE,"E5.3.0"),sQuery(id+"F0.wireOp",EDGE,"E5.4.0"),sQuery(id+"F0.wireOp",EDGE,"E5.5.0"),sQuery(id+"F0.wireOp",EDGE,"E5.6.0"),sQuery(id+"F0.wireOp",EDGE,"E5.7.0"),sQuery(id+"F0.wireOp",EDGE,"E6")])]});
            booleanBodies(context, id + "F16", {"operationType" : BooleanOperationType.SUBTRACTION, "tools" : qUnion([Q0, Q1]), "targets" : qUnion([Q2])});
        }
        {
            var Q0;
            Q0=qCreatedBy(makeId("Front.planeOp"),FACE);
            var Q1;
            Q1=sQuery(id+"F0.wireOp",VERTEX,"E5.7.0.center");
            cPlane(context, id + "F17", {"entities" : qUnion([Q0, Q1]), "cplaneType" : CPlaneType.PLANE_POINT, "offset" : 25 * mm, "width" : 150 * mm, "height" : 150 * mm});
        }
        {
            var Q0;
            Q0=qCreatedBy(id+"F17.planeOp",FACE);
            var sketch = newSketch(context, id + "F18", { "sketchPlane" : qUnion([Q0])});
            skPoint(sketch, "E41.0", {"position": v(17.68, 0) * mm});
            skPoint(sketch, "E41.1", {"position": v(-17.68, 0) * mm});
            skLineSegment(sketch, "E42", {"start": v(17.68, 20.69) * mm, "end": v(17.68, -19.13) * mm, "construction": true});
            skLineSegment(sketch, "E43", {"start": v(-17.68, 22.25) * mm, "end": v(-17.68, -19.13) * mm, "construction": true});
            skPoint(sketch, "E44", {"position": v(17.68, 5) * mm});
            skPoint(sketch, "E45", {"position": v(-17.68, 5) * mm});
            skPoint(sketch, "E46", {"position": v(17.68, -5) * mm});
            skPoint(sketch, "E47", {"position": v(-17.68, -5) * mm});
            skArc(sketch, "E48", {"start": v(17.68, -5) * mm, "mid": v(22.68, 0) * mm, "end": v(17.68, 5) * mm});
            skArc(sketch, "E49", {"start": v(-17.68, 5) * mm, "mid": v(-22.68, 0) * mm, "end": v(-17.68, -5) * mm});
            skLineSegment(sketch, "E50", {"start": v(17.68, 5) * mm, "end": v(17.68, -5) * mm});
            skLineSegment(sketch, "E51", {"start": v(-17.68, 5) * mm, "end": v(-17.68, -5) * mm});
            skSolve(sketch);
        }
        {
            var Q0;
            Q0=makeQuery(id+"F18.imprint","IMPRINT",FACE,{"disambiguationData":[TD([[makeQuery(id+"F18.imprint","IMPRINT",EDGE,{"derivedFrom":sQuery(id+"F18.wireOp",EDGE,"E48")}),1.0]])]});
            var Q1;
            Q1=sQuery(id+"F18.wireOp",EDGE,"E42");
            revolve(context, id + "F19", {"entities" : qUnion([Q0]), "axis" : qUnion([Q1]), "revolveType" : RevolveType.FULL});
        }
        {
            var Q0;
            Q0=makeQuery(id+"F18.imprint","IMPRINT",FACE,{"disambiguationData":[TD([[makeQuery(id+"F18.imprint","IMPRINT",EDGE,{"derivedFrom":sQuery(id+"F18.wireOp",EDGE,"E49")}),1.0]])]});
            var Q1;
            Q1=sQuery(id+"F18.wireOp",EDGE,"E43");
            revolve(context, id + "F20", {"entities" : qUnion([Q0]), "axis" : qUnion([Q1]), "revolveType" : RevolveType.FULL});
        }
        {
            var Q0;
            Q0=makeQuery(id+"F20.opRevolve","SWEPT_BODY",BODY,{"disambiguationData":[OSD([sQuery(id+"F18.wireOp",EDGE,"E49"),sQuery(id+"F18.wireOp",EDGE,"E51")])]});
            var Q1;
            Q1=makeQuery(id+"F19.opRevolve","SWEPT_BODY",BODY,{"disambiguationData":[OSD([sQuery(id+"F18.wireOp",EDGE,"E48"),sQuery(id+"F18.wireOp",EDGE,"E50")])]});
            var Q2;
            Q2=makeQuery(id+"F1.opExtrude","SWEPT_BODY",BODY,{"disambiguationData":[OSD([sQuery(id+"F0.wireOp",EDGE,"E0"),sQuery(id+"F0.wireOp",EDGE,"E2"),sQuery(id+"F0.wireOp",EDGE,"E3.1.0"),sQuery(id+"F0.wireOp",EDGE,"E3.2.0"),sQuery(id+"F0.wireOp",EDGE,"E3.3.0"),sQuery(id+"F0.wireOp",EDGE,"E3.4.0"),sQuery(id+"F0.wireOp",EDGE,"E3.5.0"),sQuery(id+"F0.wireOp",EDGE,"E3.6.0"),sQuery(id+"F0.wireOp",EDGE,"E3.7.0"),sQuery(id+"F0.wireOp",EDGE,"E4"),sQuery(id+"F0.wireOp",EDGE,"E5.1.0"),sQuery(id+"F0.wireOp",EDGE,"E5.2.0"),sQuery(id+"F0.wireOp",EDGE,"E5.3.0"),sQuery(id+"F0.wireOp",EDGE,"E5.4.0"),sQuery(id+"F0.wireOp",EDGE,"E5.5.0"),sQuery(id+"F0.wireOp",EDGE,"E5.6.0"),sQuery(id+"F0.wireOp",EDGE,"E5.7.0"),sQuery(id+"F0.wireOp",EDGE,"E6")])]});
            booleanBodies(context, id + "F21", {"operationType" : BooleanOperationType.SUBTRACTION, "tools" : qUnion([Q0, Q1]), "targets" : qUnion([Q2])});
        }
        {
            var Q0;
            Q0=makeQuery(id+"F1.opExtrude","CAP_FACE",FACE,{"disambiguationData":[OSD([sQuery(id+"F0.wireOp",EDGE,"E0"),sQuery(id+"F0.wireOp",EDGE,"E2"),sQuery(id+"F0.wireOp",EDGE,"E3.1.0"),sQuery(id+"F0.wireOp",EDGE,"E3.2.0"),sQuery(id+"F0.wireOp",EDGE,"E3.3.0"),sQuery(id+"F0.wireOp",EDGE,"E3.4.0"),sQuery(id+"F0.wireOp",EDGE,"E3.5.0"),sQuery(id+"F0.wireOp",EDGE,"E3.6.0"),sQuery(id+"F0.wireOp",EDGE,"E3.7.0"),sQuery(id+"F0.wireOp",EDGE,"E4"),sQuery(id+"F0.wireOp",EDGE,"E5.1.0"),sQuery(id+"F0.wireOp",EDGE,"E5.2.0"),sQuery(id+"F0.wireOp",EDGE,"E5.3.0"),sQuery(id+"F0.wireOp",EDGE,"E5.4.0"),sQuery(id+"F0.wireOp",EDGE,"E5.5.0"),sQuery(id+"F0.wireOp",EDGE,"E5.6.0"),sQuery(id+"F0.wireOp",EDGE,"E5.7.0"),sQuery(id+"F0.wireOp",EDGE,"E6")])],"isStart":false});
            var sketch = newSketch(context, id + "F22", { "sketchPlane" : qUnion([Q0])});
            skCircle(sketch, "E52.0", {"center": v(0, 0) * mm, "radius": 11.1 * mm});
            skCircle(sketch, "E53.0", {"center": v(0, 0) * mm, "radius": 15.1 * mm});
            skSolve(sketch);
        }
        {
            var Q0;
            Q0=makeQuery(id+"F22.imprint","IMPRINT",FACE,{"disambiguationData":[TD([[makeQuery(id+"F22.imprint","IMPRINT",EDGE,{"derivedFrom":sQuery(id+"F22.wireOp",EDGE,"E52.0")}),-1.0]])]});
            extrude(context, id + "F23", {"entities" : qUnion([Q0]), "operationType" : NewBodyOperationType.ADD, "depth" : 3 * mm});
        }
        {
            var Q0;
            Q0=makeQuery(id+"F23.opExtrude","CAP_EDGE",EDGE,{"disambiguationData":[OSD([sQuery(id+"F22.wireOp",EDGE,"E53.0")])],"isStart":false});
            chamfer(context, id + "F24", {"entities" : qUnion([Q0]), "width" : 3 * mm, "tangentPropagation" : true});
        }
        {
            var Q0;
            Q0=makeQuery(id+"F24.opChamfer","BLEND_EDGE",EDGE,{"blendedFrom":[makeQuery(id+"F23.opExtrude","CAP_EDGE",EDGE,{"disambiguationData":[OSD([sQuery(id+"F22.wireOp",EDGE,"E53.0")])],"isStart":false}),makeQuery(id+"F1.opExtrude","CAP_FACE",FACE,{"disambiguationData":[OSD([sQuery(id+"F0.wireOp",EDGE,"E0"),sQuery(id+"F0.wireOp",EDGE,"E2"),sQuery(id+"F0.wireOp",EDGE,"E3.1.0"),sQuery(id+"F0.wireOp",EDGE,"E3.2.0"),sQuery(id+"F0.wireOp",EDGE,"E3.3.0"),sQuery(id+"F0.wireOp",EDGE,"E3.4.0"),sQuery(id+"F0.wireOp",EDGE,"E3.5.0"),sQuery(id+"F0.wireOp",EDGE,"E3.6.0"),sQuery(id+"F0.wireOp",EDGE,"E3.7.0"),sQuery(id+"F0.wireOp",EDGE,"E4"),sQuery(id+"F0.wireOp",EDGE,"E5.1.0"),sQuery(id+"F0.wireOp",EDGE,"E5.2.0"),sQuery(id+"F0.wireOp",EDGE,"E5.3.0"),sQuery(id+"F0.wireOp",EDGE,"E5.4.0"),sQuery(id+"F0.wireOp",EDGE,"E5.5.0"),sQuery(id+"F0.wireOp",EDGE,"E5.6.0"),sQuery(id+"F0.wireOp",EDGE,"E5.7.0"),sQuery(id+"F0.wireOp",EDGE,"E6")])],"isStart":false})],"blendedInto":[makeQuery(id+"F1.opExtrude","CAP_FACE",FACE,{"disambiguationData":[OSD([sQuery(id+"F0.wireOp",EDGE,"E0"),sQuery(id+"F0.wireOp",EDGE,"E2"),sQuery(id+"F0.wireOp",EDGE,"E3.1.0"),sQuery(id+"F0.wireOp",EDGE,"E3.2.0"),sQuery(id+"F0.wireOp",EDGE,"E3.3.0"),sQuery(id+"F0.wireOp",EDGE,"E3.4.0"),sQuery(id+"F0.wireOp",EDGE,"E3.5.0"),sQuery(id+"F0.wireOp",EDGE,"E3.6.0"),sQuery(id+"F0.wireOp",EDGE,"E3.7.0"),sQuery(id+"F0.wireOp",EDGE,"E4"),sQuery(id+"F0.wireOp",EDGE,"E5.1.0"),sQuery(id+"F0.wireOp",EDGE,"E5.2.0"),sQuery(id+"F0.wireOp",EDGE,"E5.3.0"),sQuery(id+"F0.wireOp",EDGE,"E5.4.0"),sQuery(id+"F0.wireOp",EDGE,"E5.5.0"),sQuery(id+"F0.wireOp",EDGE,"E5.6.0"),sQuery(id+"F0.wireOp",EDGE,"E5.7.0"),sQuery(id+"F0.wireOp",EDGE,"E6")])],"isStart":false})]});
            var Q1;
            {var subQ0=sQuery(id+"F22.wireOp",EDGE,"E53.0");Q1=makeQuery(id+"F24.opChamfer","BLEND_EDGE",EDGE,{"blendedFrom":[makeQuery(id+"F23.opExtrude","CAP_EDGE",EDGE,{"disambiguationData":[OSD([subQ0])],"isStart":false}),makeQuery(id+"F23.opExtrude","CAP_FACE",FACE,{"disambiguationData":[OSD([sQuery(id+"F22.wireOp",EDGE,"E52.0"),subQ0])],"isStart":false})],"blendedInto":[makeQuery(id+"F23.opExtrude","CAP_FACE",FACE,{"disambiguationData":[OSD([sQuery(id+"F22.wireOp",EDGE,"E52.0"),subQ0])],"isStart":false})]});}
            fillet(context, id + "F25", {"entities" : qUnion([Q0, Q1]), "radius" : .75 * mm, "tangentPropagation" : true, "allowEdgeOverflow" : false});
        }
    });
